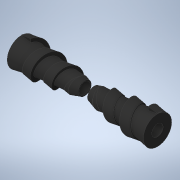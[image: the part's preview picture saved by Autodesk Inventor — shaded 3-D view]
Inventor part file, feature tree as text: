
AUTODESK INVENTOR PART (.ipt)
format: ipt  version: 2022 (Build 260153000, 153)  size: 460,288 bytes
history: native  units: mm
features: sketch x9, extrude x5, revolve x3, other x2, mirror x2, projected_geometry x2, helix x1
ambient origin geometry x8: Origin, YZ Plane, XZ Plane, XY Plane, X Axis, Y Axis, Z Axis, Center Point
bodies: Volumenkörper1 (feature_tree), Solid2 (feature_tree), Solid3 (feature_tree)
feature tree (24):
  other  "Dribblerschnecke2"
  extrude  "Extrusion1"  Depth=11.0mm
  other  "Spirale1"
  mirror  "Spiegeln1"
  extrude  "Extrusion5"  Depth=10.0mm
  extrude  "Extrusion6"  Depth=1.0mm
  sketch  "Sketch9"  dims[d19=0.1mm d32=10.0mm d33=0.0mm]
  revolve  "Revolution1"  [1 undecoded]
  revolve  "Revolution2"  [1 undecoded]
  helix  "Coil2"  [1 undecoded]
  mirror  "Mirror2"
  extrude  "Extrusion7"  Depth=2.0mm
  extrude  "Extrusion8"  TaperAngle=90.0deg  [1 undecoded]
  revolve  "Revolution3"  [1 undecoded]
  sketch  "Skizze1"  dims[d0=6.0mm d1=11.0mm]
  sketch  "Skizze3"  dims[d2=36.0mm d3=0.0mm]
  projected_geometry  "Projizierte Kontur2"
  sketch  "Sketch7"  dims[d8=7.0mm d9=24.5mm d10=10.0mm d11=0.0mm d12=90.0deg d13=90.0deg d14=0.0mm d15=0.0mm d16=4.0mm]
  sketch  "Sketch8"  dims[d17=13.962634mm d18=1.0mm]
  projected_geometry  "Projected Loop4"
  sketch  "Sketch10"  dims[d34=7.0mm d35=100.0mm d36=0.0mm d37=82.0mm d38=0.0mm]
  sketch  "Sketch11"  dims[d41=2.0mm d42=2.0mm]
  sketch  "Sketch12"  dims[d43=200.0mm d44=90.0deg]
  sketch  "Sketch13"  dims[d45=90.0deg d47=0.0mm d48=13.962634mm d49=5.0mm d50=2.2mm d51=0.6mm d53=10.0mm d54=10.0mm d55=30.0mm d56=-1.204277mm d57=90.0deg d58=90.0deg d59=0.0mm d60=0.0mm d61=13.962634mm d62=7.1mm d63=80.0mm d64=0.0mm d65=15.0mm d66=5.0mm d67=0.0mm d68=3.5mm d69=3.5mm d70=360.0deg d71=1.0mm d72=0.0mm]
note: 5 required parameter values undecoded (feature->parameter linkage not recoverable at this tier; creation-order binding heuristic only, values carry confidence <= 0.55)